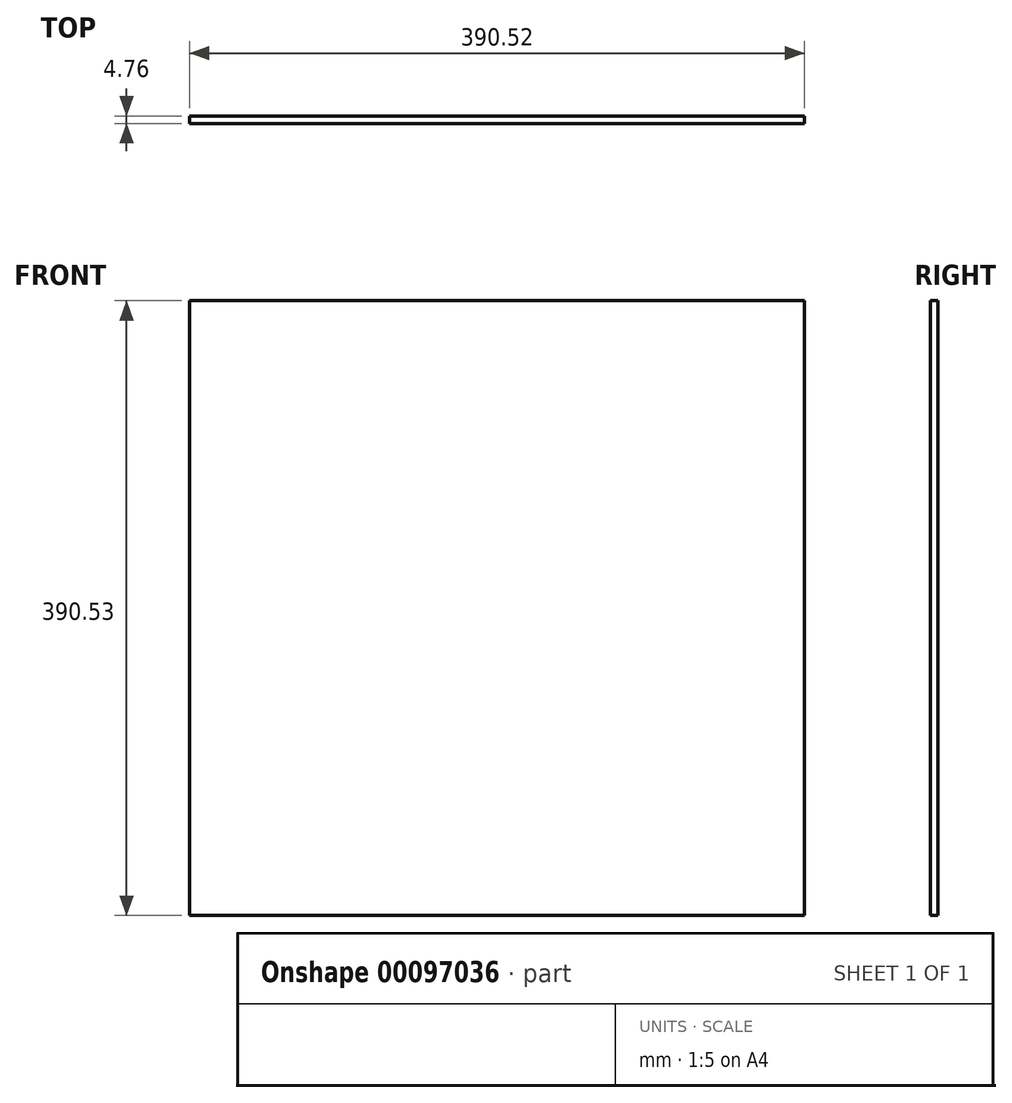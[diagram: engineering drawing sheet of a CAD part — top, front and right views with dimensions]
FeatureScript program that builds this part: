
annotation { "Feature Type Name" : "Feature", "Feature Type Description" : "" }
export const myFeature = defineFeature(function(context is Context, id is Id, definition is map)
    precondition{}
    {
        {
            var Q0;
            Q0=qCreatedBy(makeId("Front.planeOp"),FACE);
            var sketch = newSketch(context, id + "F0", { "sketchPlane" : qUnion([Q0])});
            skLineSegment(sketch, "E0.bottom", {"start": v(-192.11, 214.96) * mm, "end": v(198.41, 214.96) * mm});
            skLineSegment(sketch, "E0.top", {"start": v(-192.11, -175.57) * mm, "end": v(198.41, -175.57) * mm});
            skLineSegment(sketch, "E0.left", {"start": v(-192.11, 214.96) * mm, "end": v(-192.11, -175.57) * mm});
            skLineSegment(sketch, "E0.right", {"start": v(198.41, 214.96) * mm, "end": v(198.41, -175.57) * mm});
            skText(sketch, "E1", { "text": "3/16 ply\n", "fontName": "OpenSans-Regular.ttf"});
            const initialGuessF0  = {"E1": [-0.0786, -0.2241, 1, 0, 0.02786]};
            skSetInitialGuess(sketch, initialGuessF0);
            skSolve(sketch);
        }
        {
            var Q0;
            Q0=makeQuery(id+"F0.imprint","IMPRINT",FACE,{"disambiguationData":[TD([[makeQuery(id+"F0.imprint","IMPRINT",EDGE,{"derivedFrom":sQuery(id+"F0.wireOp",EDGE,"E0.bottom")}),-1.0]])]});
            extrude(context, id + "F1", {"entities" : qUnion([Q0]), "endBound" : BoundingType.SYMMETRIC, "depth" : 4.76 * mm});
        }
    });
